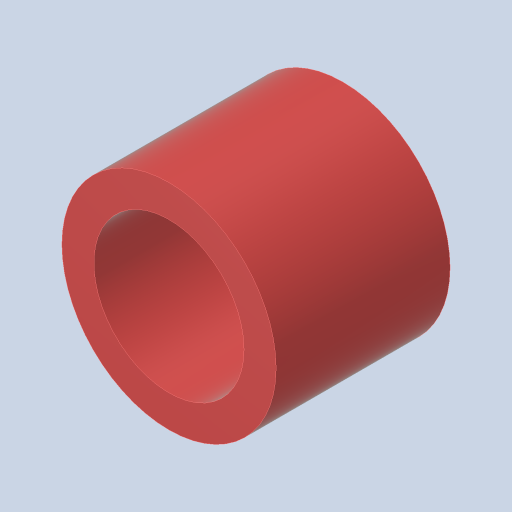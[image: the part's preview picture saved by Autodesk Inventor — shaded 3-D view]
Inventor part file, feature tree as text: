
AUTODESK INVENTOR PART (.ipt)
format: ipt  version: 2023.4 (Build 274418000, 418)  size: 120,832 bytes
history: native  units: in
note: dims shown in document units (in); Inventor stores cm internally (conversion verified against a paired STEP export)
features: extrude x1, sketch x1
ambient origin geometry x8: Origin, YZ Plane, XZ Plane, XY Plane, X Axis, Y Axis, Z Axis, Center Point
bodies: Solid1 (feature_tree)
feature tree (2):
  extrude  "Extrusion1"  Depth=0.678in
  sketch  "Sketch1"  dims[d0=0.585in d1=0.125in d2=0.678in d3=0.0in]
